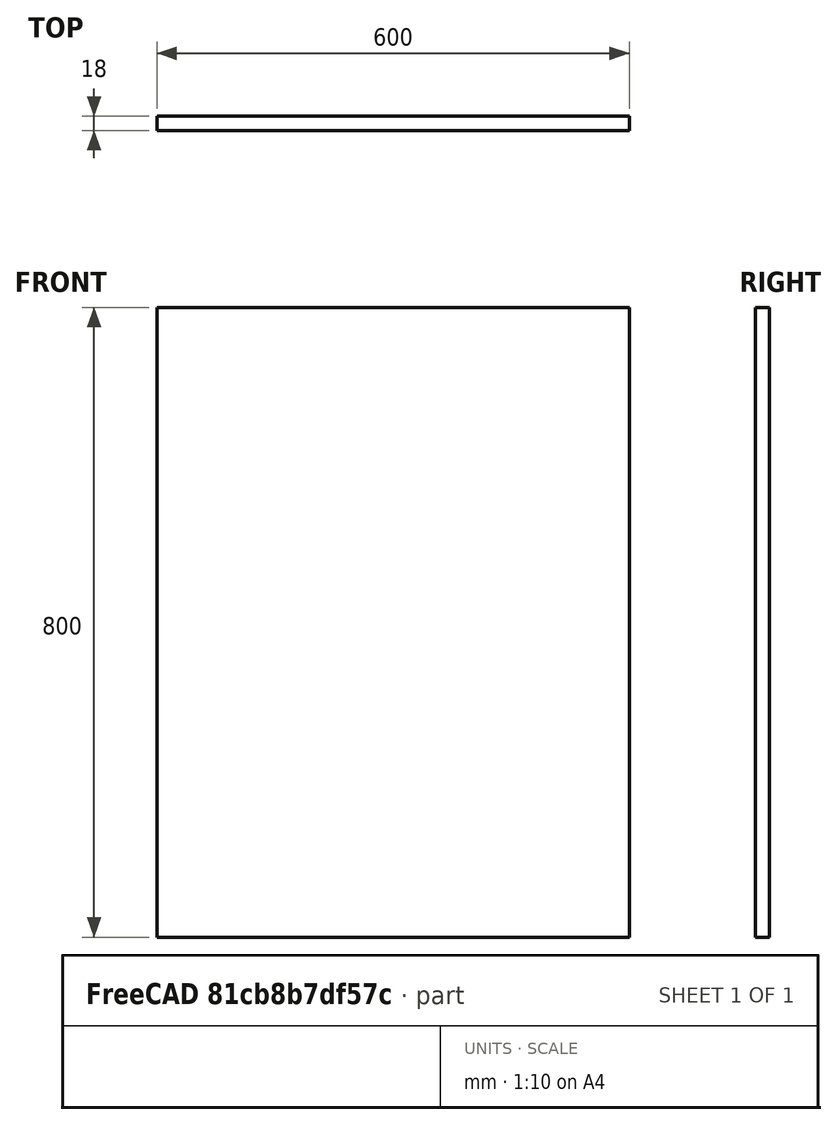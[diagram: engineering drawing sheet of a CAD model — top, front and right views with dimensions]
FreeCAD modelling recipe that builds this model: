
FCSTD DOCUMENT  (FreeCAD 0.18R4 (GitTag))
Label: back
License: All rights reserved
LicenseURL: http://en.wikipedia.org/wiki/All_rights_reserved
objects: Sketcher::SketchObject×1, PartDesign::Pad×1, PartDesign::Body×1
note: 4 computed .brp shape members not serialized (recipe doc carries the construction recipe); baked Part::Feature solids carry a one-line shape summary decoded from their .brp

FEATURE [Sketcher::SketchObject] Sketch
  MapMode = 5
  Placement = pos=(0,0,0) rot=(1,0,0;1.5708rad)
  Support = -> [XZ_Plane]
  sketch-geometry (4):
    g0: LineSegment StartX=0 StartY=0 StartZ=0 EndX=-600 EndY=0 EndZ=0
    g1: LineSegment StartX=-600 StartY=0 StartZ=0 EndX=-600 EndY=800 EndZ=0
    g2: LineSegment StartX=-600 StartY=800 StartZ=0 EndX=0 EndY=800 EndZ=0
    g3: LineSegment StartX=0 StartY=800 StartZ=0 EndX=0 EndY=0 EndZ=0
  constraints (11):
    c: Coincident(g0,g1)
    c: Coincident(g1,g2)
    c: Coincident(g2,g3)
    c: Coincident(g3,g0)
    c: Horizontal(g0)
    c: Horizontal(g2)
    c: Vertical(g1)
    c: Vertical(g3)
    c: Coincident(g0,g-1)
    c: DistanceY(g3,g3) = 800
    c: DistanceX(g0,g0) = 600
FEATURE [PartDesign::Pad] Pad
  Length = 18
  Length2 = 100
  Placement = pos=(0,0,0) rot=(1,0,0;1.5708rad)
  Profile = -> Sketch
  Type = 0
FEATURE [PartDesign::Body] Body
  Group = -> [Sketch,Pad]
  Origin = -> Origin
  Tip = -> Pad
